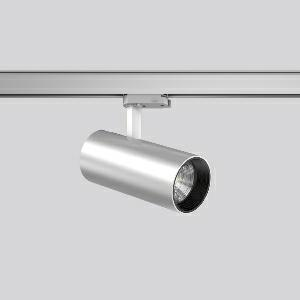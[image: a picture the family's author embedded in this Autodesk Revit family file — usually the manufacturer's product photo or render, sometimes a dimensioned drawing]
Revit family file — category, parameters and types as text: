
# Revit family: deecos_s_mini_742206_004_3_76_58c3
name_source: partatom
category: Lighting Fixtures
units: mm (PartAtom-declared; Revit-internal decimal feet)

## family parameters
Cut with Voids When Loaded = No
Host = Face
Light Source = No
Part Type = Normal
Room Calculation Point = No
Round Connector Dimension = Use Diameter
Shared = No

## types (1)
- DEECOS S mini (1 x LED Modul 935, 3250 lm, 3500)
    Apparent Load = 29 VA
    Approval mark = CE
    CIE Flux Codes = 99 100 100 100 100
    Color Rendering = 92
    Color Temperature = 3500
    Default Elevation = 1800 mm
    Description = Series: DEECOS S mini
LED surface-mounted projector in modern design with no visible cooling ribs. Housing: die-cast aluminium, powder-coated. Rotation range: 356°. Swivel range: 90°. Black plastic ring and recessed LED to prevent glare from the side. Optical assembly with lens made of plastic (polycarbonate) for the best homogeneous light distribution - can be changed without tools. Best colour rendering index Ra>90. With adapter for RZB 3-circuit DALI tracks. Suitable for Track on ceiling, Wall track. High quality converter without flickering and stroboscopic effect. The following accessories can be mounted without use of tools: interchangeable lenses, decorative glasses, honeycomb louvre, clear and frosted diffusers, white interchangeable plastic ring. 
Colour: silver
Diameter: 87 mm
Height: 214 mm
Lamp: LED
Socket: without socket
Colour temperature: 3500K
Colour rendering index (CRI): 92
System power: 29 W
Rated luminous flux: 3250 lm
Luminous efficiency: 112 lm/W
Control gear: Converter, dimmable, DALI
Protection class: I
Type of protection: IP 20
    Height = 214 mm
    Lamp = 1 x LED Modul 935
    Lamp Light Flux = 3250 lm
    Lamp count = 1
    Length = 87 mm
    Lifetime = 50000 h
    Luminous efficacy = 112 lm/W
    Manufacturer = RZB
    ModVariant = No
    Model = 742206.004.3.76
    Mounting Place = Ceiling
    Mounting Type = Rail mounted
    Number of Poles = 1
    OnlyDefault = Yes
    Power Factor = 1
    Product Name = DEECOS S mini
    Product group = Track mounted projectors
    ProductGroupID = 301
    Protection Class = Protection class I
    Protection Degree = IP 20
    RLX_Detail_Level = 1
    RLX_Emergency_Light_Flux = 0 lm
    RLX_Emergency_Type = 0
    RLX_Emergency_Type_DB = No
    RlxData = <blob elided: 37393 chars, md5=68657926>
    Socket = socket
    Standby Power = 0 W
    System Light Flux = 3250 lm
    System Power = 29 W
    Type Comments = Product without accessories
    Type Image = 741930.004.jpg
    URL = http://relux.com
    VarID = ---
    Voltage = 230 V
    Voltage Range = 220-240 V
    Weight = 0.00 kg
    Width = 0 mm  [stored 0 ft]

note: [stored X ft] marks values corroborated as IEEE doubles in the binary element streams (Revit-internal decimal feet)

## geometry (parser evidence)
native form markers: Blend x4, Sweep x13
no freeform markers — native parametric forms only
